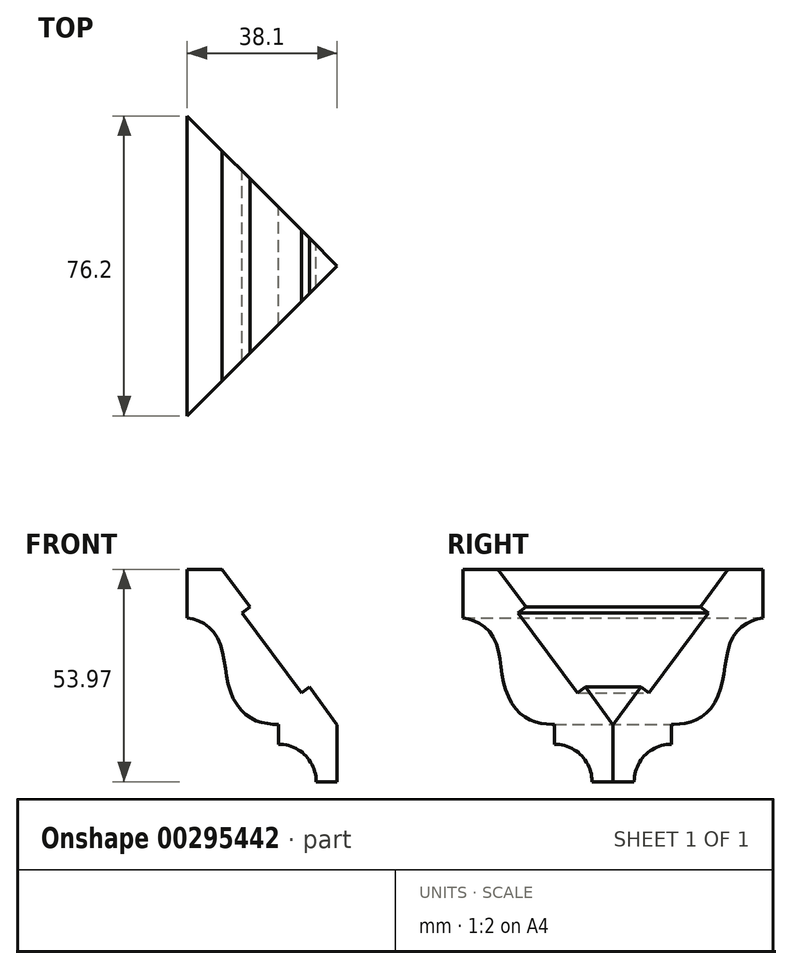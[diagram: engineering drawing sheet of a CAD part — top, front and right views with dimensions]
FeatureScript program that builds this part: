
annotation { "Feature Type Name" : "Feature", "Feature Type Description" : "" }
export const myFeature = defineFeature(function(context is Context, id is Id, definition is map)
    precondition{}
    {
        {
            var Q0;
            Q0=qCreatedBy(makeId("Front.planeOp"),FACE);
            var sketch = newSketch(context, id + "F0", { "sketchPlane" : qUnion([Q0])});
            skLineSegment(sketch, "E0", {"start": v(12.7, -24.07) * mm, "end": v(18.04, -24.07) * mm});
            skLineSegment(sketch, "E1", {"start": v(18.04, -24.07) * mm, "end": v(18.04, -9.6) * mm});
            skLineSegment(sketch, "E2", {"start": v(-11.17, 29.9) * mm, "end": v(-20.06, 29.9) * mm});
            skLineSegment(sketch, "E3", {"start": v(-20.06, 29.9) * mm, "end": v(-20.06, 17.58) * mm});
            skLineSegment(sketch, "E4", {"start": v(18.04, -9.6) * mm, "end": v(10.99, -0.06) * mm});
            skLineSegment(sketch, "E5", {"start": v(10.99, -0.06) * mm, "end": v(8.95, -1.57) * mm});
            skLineSegment(sketch, "E6", {"start": v(8.95, -1.57) * mm, "end": v(-6.16, 18.85) * mm});
            skLineSegment(sketch, "E7", {"start": v(-6.16, 18.85) * mm, "end": v(-4.11, 20.36) * mm});
            skLineSegment(sketch, "E8", {"start": v(-4.11, 20.36) * mm, "end": v(-11.17, 29.9) * mm});
            skLineSegment(sketch, "E9", {"start": v(3.18, -14.55) * mm, "end": v(3.18, -9.47) * mm});
            skArc(sketch, "E10", {"start": v(12.7, -24.07) * mm, "mid": v(9.92, -17.34) * mm, "end": v(3.18, -14.55) * mm});
            skFitSpline(sketch, "E11", {"points": [v(-20.06, 17.58) * mm, v(-9.82, 1.52) * mm, v(3.18, -9.47) * mm], "startDerivative": vector(58.03, -11.78) * mm, "endDerivative": vector(50.48, 1.67) * mm});
            skPoint(sketch, "E12.orphan", {"position": v(-20.06, -24.07) * mm});
            skSolve(sketch);
        }
        {
            var Q0;
            Q0 = qSketchRegion(id + "F0", true);
            extrude(context, id + "F1", {"entities" : qUnion([Q0]), "endBound" : BoundingType.SYMMETRIC, "depth" : 152.4 * mm});
        }
        {
            var Q0;
            Q0=qCreatedBy(makeId("Top.planeOp"),FACE);
            var sketch = newSketch(context, id + "F2", { "sketchPlane" : qUnion([Q0])});
            skLineSegment(sketch, "E13", {"start": v(-20.06, 38.1) * mm, "end": v(-20.06, -38.1) * mm});
            skLineSegment(sketch, "E14", {"start": v(-20.06, -38.1) * mm, "end": v(18.04, 0) * mm});
            skLineSegment(sketch, "E15", {"start": v(18.04, 0) * mm, "end": v(-20.06, 38.1) * mm});
            skSolve(sketch);
        }
        {
            var Q0;
            Q0 = qSketchRegion(id + "F2", true);
            extrude(context, id + "F3", {"entities" : qUnion([Q0]), "operationType" : NewBodyOperationType.INTERSECT, "endBound" : BoundingType.SYMMETRIC, "depth" : 127 * mm});
        }
    });
